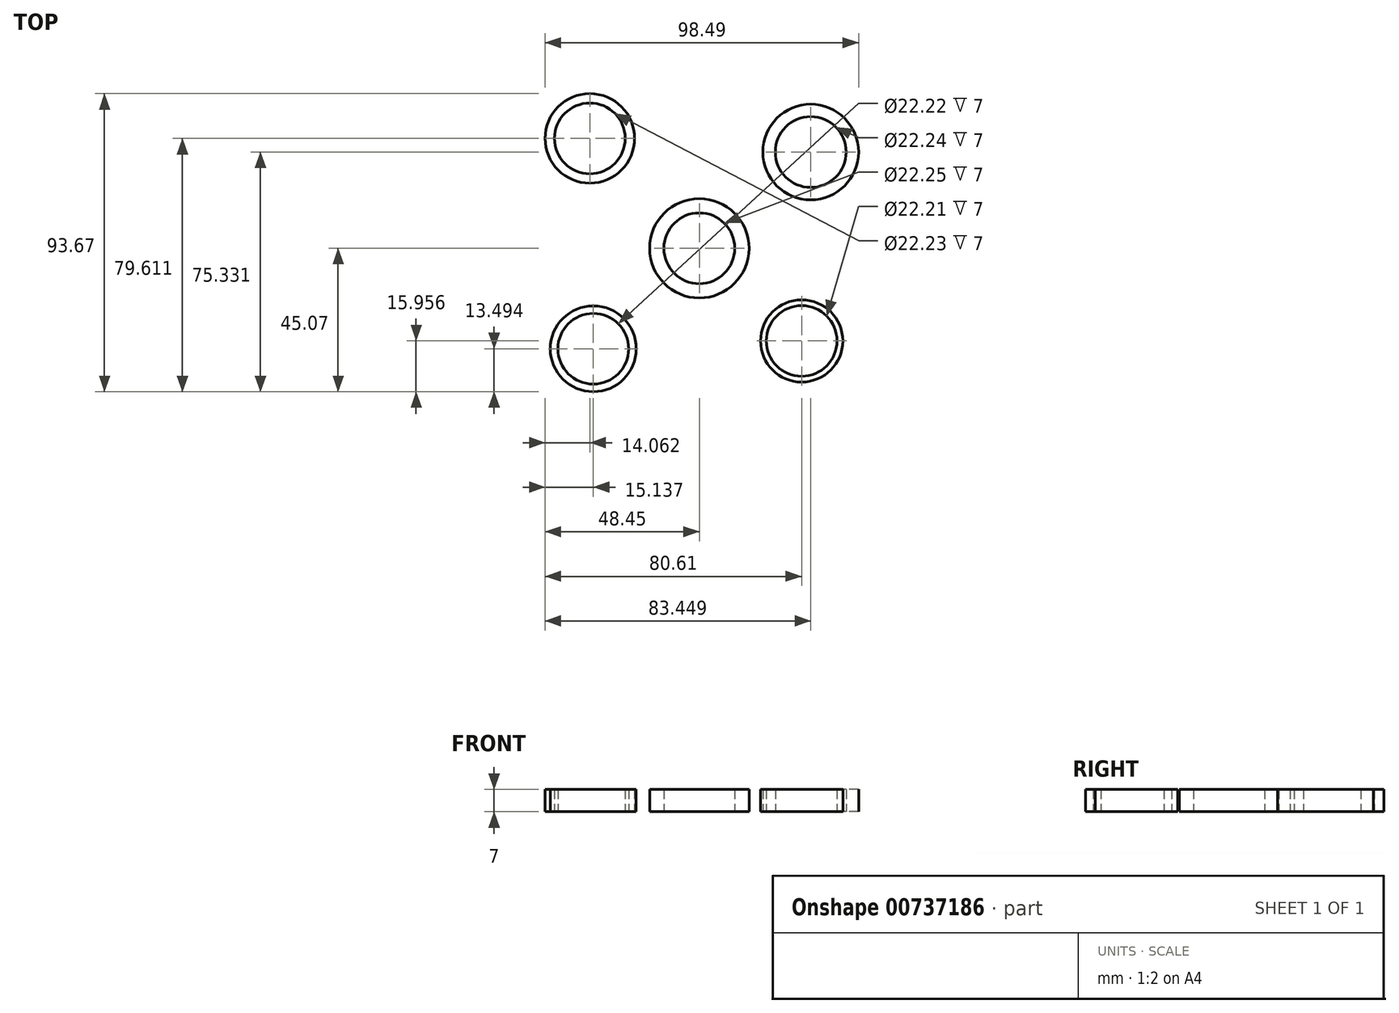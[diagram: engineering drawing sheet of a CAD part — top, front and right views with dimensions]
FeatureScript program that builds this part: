
annotation { "Feature Type Name" : "Feature", "Feature Type Description" : "" }
export const myFeature = defineFeature(function(context is Context, id is Id, definition is map)
    precondition{}
    {
        {
            var Q0;
            Q0=qCreatedBy(makeId("Top.planeOp"),FACE);
            var sketch = newSketch(context, id + "F0", { "sketchPlane" : qUnion([Q0])});
            skCircle(sketch, "E0", {"center": v(0, 0) * mm, "radius": 11.12 * mm});
            skCircle(sketch, "E1", {"center": v(0, 0) * mm, "radius": 15.62 * mm});
            skCircle(sketch, "E2", {"center": v(35, 30.26) * mm, "radius": 11.12 * mm});
            skCircle(sketch, "E3", {"center": v(35, 30.26) * mm, "radius": 15.04 * mm});
            skCircle(sketch, "E4", {"center": v(-34.39, 34.54) * mm, "radius": 11.12 * mm});
            skCircle(sketch, "E5", {"center": v(-34.39, 34.54) * mm, "radius": 14.06 * mm});
            skCircle(sketch, "E6", {"center": v(-33.31, -31.58) * mm, "radius": 11.1 * mm});
            skCircle(sketch, "E7", {"center": v(-33.31, -31.58) * mm, "radius": 13.5 * mm});
            skCircle(sketch, "E8", {"center": v(32.16, -29.11) * mm, "radius": 11.1 * mm});
            skCircle(sketch, "E9", {"center": v(32.16, -29.11) * mm, "radius": 12.92 * mm});
            skSolve(sketch);
        }
        {
            var Q0;
            Q0=makeQuery(id+"F0.imprint","IMPRINT",FACE,{"disambiguationData":[TD([[makeQuery(id+"F0.imprint","IMPRINT",EDGE,{"derivedFrom":sQuery(id+"F0.wireOp",EDGE,"E4")}),-1.0]])]});
            var Q1;
            Q1=makeQuery(id+"F0.imprint","IMPRINT",FACE,{"disambiguationData":[TD([[makeQuery(id+"F0.imprint","IMPRINT",EDGE,{"derivedFrom":sQuery(id+"F0.wireOp",EDGE,"E2")}),-1.0]])]});
            var Q2;
            Q2=makeQuery(id+"F0.imprint","IMPRINT",FACE,{"disambiguationData":[TD([[makeQuery(id+"F0.imprint","IMPRINT",EDGE,{"derivedFrom":sQuery(id+"F0.wireOp",EDGE,"E0")}),-1.0]])]});
            var Q3;
            Q3=makeQuery(id+"F0.imprint","IMPRINT",FACE,{"disambiguationData":[TD([[makeQuery(id+"F0.imprint","IMPRINT",EDGE,{"derivedFrom":sQuery(id+"F0.wireOp",EDGE,"E6")}),-1.0]])]});
            var Q4;
            Q4=makeQuery(id+"F0.imprint","IMPRINT",FACE,{"disambiguationData":[TD([[makeQuery(id+"F0.imprint","IMPRINT",EDGE,{"derivedFrom":sQuery(id+"F0.wireOp",EDGE,"E8")}),-1.0]])]});
            extrude(context, id + "F1", {"entities" : qUnion([Q0, Q1, Q2, Q3, Q4]), "depth" : 7 * mm, "offsetDistance" : 25 * mm});
        }
    });
